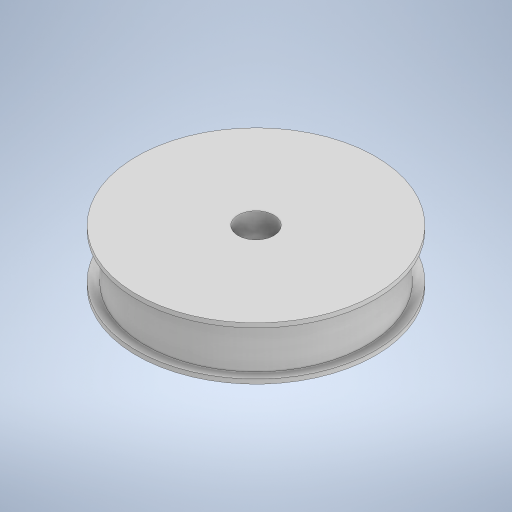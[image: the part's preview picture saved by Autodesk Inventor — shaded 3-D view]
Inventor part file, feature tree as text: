
AUTODESK INVENTOR PART (.ipt)
format: ipt  version: 2023 (Build 270158000, 158)  size: 240,128 bytes
history: native  units: mm
features: extrude x4, sketch x4, other x1
ambient origin geometry x8: Origin, YZ Plane, XZ Plane, XY Plane, X Axis, Y Axis, Z Axis, Center Point
bodies: Body1 (feature_tree)
feature tree (9):
  other  "ソリッド1"
  extrude  "押し出し1"  Depth=50.0mm
  extrude  "押し出し2"  Depth=10.0mm TaperAngle=0.0deg
  extrude  "押し出し3"  Depth=54.0mm
  extrude  "押し出し4"  Depth=1.0mm TaperAngle=0.0deg
  sketch  "スケッチ1"
  sketch  "スケッチ2"
  sketch  "スケッチ3"
  sketch  "スケッチ4"
